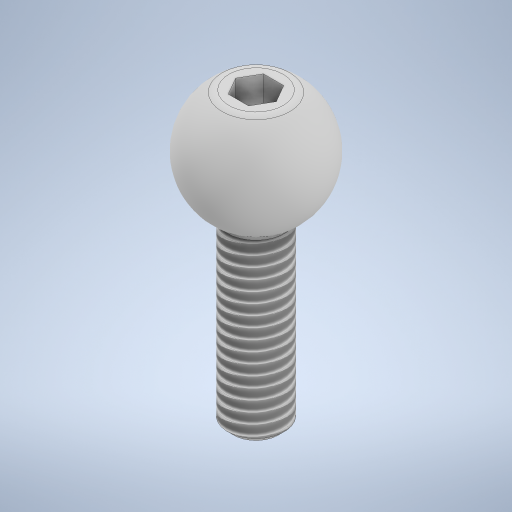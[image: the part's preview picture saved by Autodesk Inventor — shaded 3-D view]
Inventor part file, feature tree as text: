
AUTODESK INVENTOR PART (.ipt)
format: ipt  version: 2024 (Build 280153000, 153)  size: 323,584 bytes
history: native  units: in
note: dims shown in document units (in); Inventor stores cm internally (conversion verified against a paired STEP export)
features: sketch x3, fillet x2, plane x2, revolve x1, chamfer x1, split x1, extrude x1, thread x1, direct_edit x1, projected_geometry x1, other x1
ambient origin geometry x8: Origin, YZ Plane, XZ Plane, XY Plane, X Axis, Y Axis, Z Axis, Center Point
bodies: Solid1 (feature_tree)
feature tree (15):
  revolve  "Revolution1"  [1 undecoded]
  fillet  "Fillet1"  Radius=0.15in
  chamfer  "Chamfer1"  Distance=0.015in Angle=45.0deg
  sketch  "Sketch2"  dims[d3=360.0deg]
  plane  "Work Plane1"
  plane  "Work Plane2"
  split  "Split1"
  fillet  "Fillet2"  [1 undecoded]
  extrude  "Extrusion1"  Depth=0.3937in
  thread  "Thread1"  [1 undecoded]
  direct_edit  "Direct Edit1"
  sketch  "Sketch1"  dims[d0=0.325in d1=0.625in d2=0.15in]
  sketch  "Sketch3"  dims[d4=0.015in d5=0.015in d6=0.125in d7=45.0deg d9=0.0in d10=0.032in d11=0.0938in d12=0.1in d13=0.0in d14=0.457in d15=0.0in d16=3.937in d17=0.3937in d18=0.3937in]
  projected_geometry  "Project Cut Edges1"
  other  "Scale1"
note: 3 required parameter values undecoded (feature->parameter linkage not recoverable at this tier; creation-order binding heuristic only, values carry confidence <= 0.55)